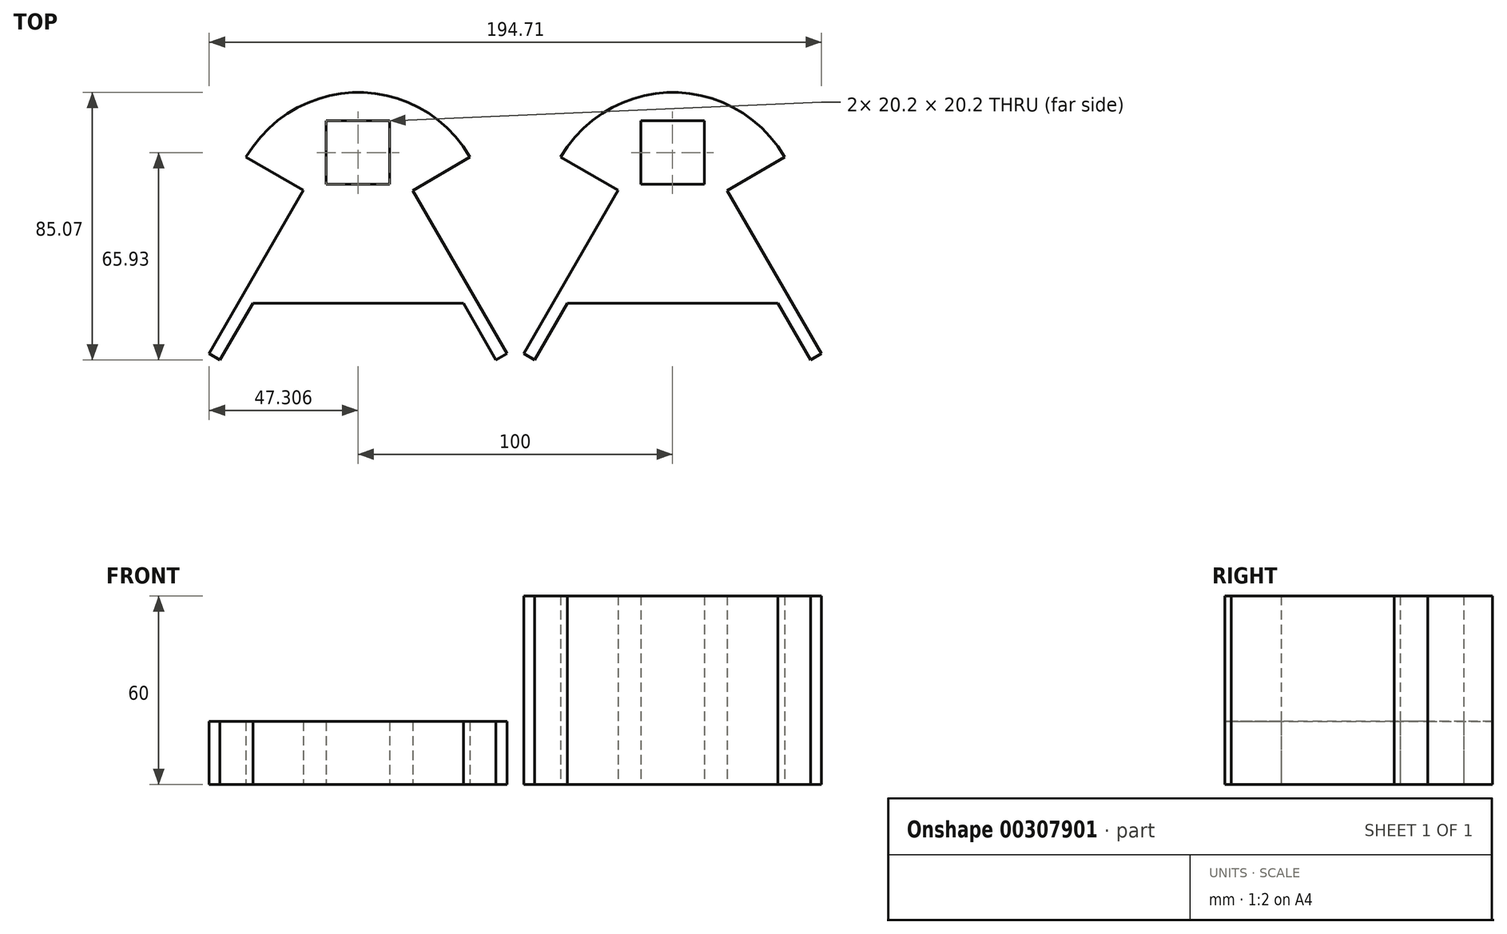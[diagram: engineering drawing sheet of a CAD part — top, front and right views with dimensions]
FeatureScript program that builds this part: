
annotation { "Feature Type Name" : "Feature", "Feature Type Description" : "" }
export const myFeature = defineFeature(function(context is Context, id is Id, definition is map)
    precondition{}
    {
        {
            var Q0;
            Q0=qCreatedBy(makeId("Top.planeOp"),FACE);
            var sketch = newSketch(context, id + "F0", { "sketchPlane" : qUnion([Q0])});
            skLineSegment(sketch, "E0", {"start": v(-35.64, 21.96) * mm, "end": v(-17.37, 11.4) * mm});
            skLineSegment(sketch, "E1", {"start": v(-17.37, 11.4) * mm, "end": v(-47.34, -40.54) * mm});
            skLineSegment(sketch, "E2", {"start": v(-47.34, -40.54) * mm, "end": v(-43.87, -42.53) * mm});
            skLineSegment(sketch, "E3", {"start": v(-43.87, -42.53) * mm, "end": v(-33.38, -24.53) * mm});
            skLineSegment(sketch, "E4", {"start": v(-33.38, -24.53) * mm, "end": v(33.53, -24.53) * mm});
            skLineSegment(sketch, "E5", {"start": v(33.53, -24.53) * mm, "end": v(43.89, -42.5) * mm});
            skLineSegment(sketch, "E6", {"start": v(43.89, -42.5) * mm, "end": v(47.37, -40.52) * mm});
            skLineSegment(sketch, "E7", {"start": v(47.37, -40.52) * mm, "end": v(17.36, 11.37) * mm});
            skLineSegment(sketch, "E8", {"start": v(17.36, 11.37) * mm, "end": v(35.63, 21.98) * mm});
            skFitSpline(sketch, "E9", {"points": [v(-35.64, 21.96) * mm, v(0, 42.54) * mm, v(35.63, 21.98) * mm], "startDerivative": vector(47.33, 80.24) * mm, "endDerivative": vector(47.32, -80.99) * mm});
            skLineSegment(sketch, "E10.bottom", {"start": v(-10.13, 33.5) * mm, "end": v(10.07, 33.5) * mm});
            skLineSegment(sketch, "E10.top", {"start": v(-10.13, 13.3) * mm, "end": v(10.07, 13.3) * mm});
            skLineSegment(sketch, "E10.left", {"start": v(-10.13, 33.5) * mm, "end": v(-10.13, 13.3) * mm});
            skLineSegment(sketch, "E10.right", {"start": v(10.07, 33.5) * mm, "end": v(10.07, 13.3) * mm});
            skSolve(sketch);
        }
        {
            var Q0;
            Q0=makeQuery(id+"F0.imprint","IMPRINT",FACE,{"disambiguationData":[TD([[makeQuery(id+"F0.imprint","IMPRINT",EDGE,{"derivedFrom":sQuery(id+"F0.wireOp",EDGE,"E0")}),1.0]])]});
            extrude(context, id + "F1", {"entities" : qUnion([Q0]), "depth" : 20 * mm});
        }
        {
            var Q0;
            Q0 = qSketchRegion(id + "F0", true);
            extrude(context, id + "F2", {"entities" : qUnion([Q0]), "depth" : 60 * mm});
        }
        {
            var Q0;
            Q0=makeQuery(id+"F2.opExtrude","SWEPT_BODY",BODY,{"disambiguationData":[OSD([sQuery(id+"F0.wireOp",EDGE,"E0"),sQuery(id+"F0.wireOp",EDGE,"E1"),sQuery(id+"F0.wireOp",EDGE,"E2"),sQuery(id+"F0.wireOp",EDGE,"E3"),sQuery(id+"F0.wireOp",EDGE,"E4"),sQuery(id+"F0.wireOp",EDGE,"E5"),sQuery(id+"F0.wireOp",EDGE,"E6"),sQuery(id+"F0.wireOp",EDGE,"E7"),sQuery(id+"F0.wireOp",EDGE,"E8"),sQuery(id+"F0.wireOp",EDGE,"E9"),sQuery(id+"F0.wireOp",EDGE,"E10.bottom"),sQuery(id+"F0.wireOp",EDGE,"E10.top"),sQuery(id+"F0.wireOp",EDGE,"E10.left"),sQuery(id+"F0.wireOp",EDGE,"E10.right")])]});
            transform(context, id + "F3", {"entities" : qUnion([Q0]), "transformType" : TransformType.TRANSLATION_3D, "dx" : 100 * mm, "dy" : 0 * mm, "dz" : 0 * mm, "makeCopy" : false});
        }
    });
